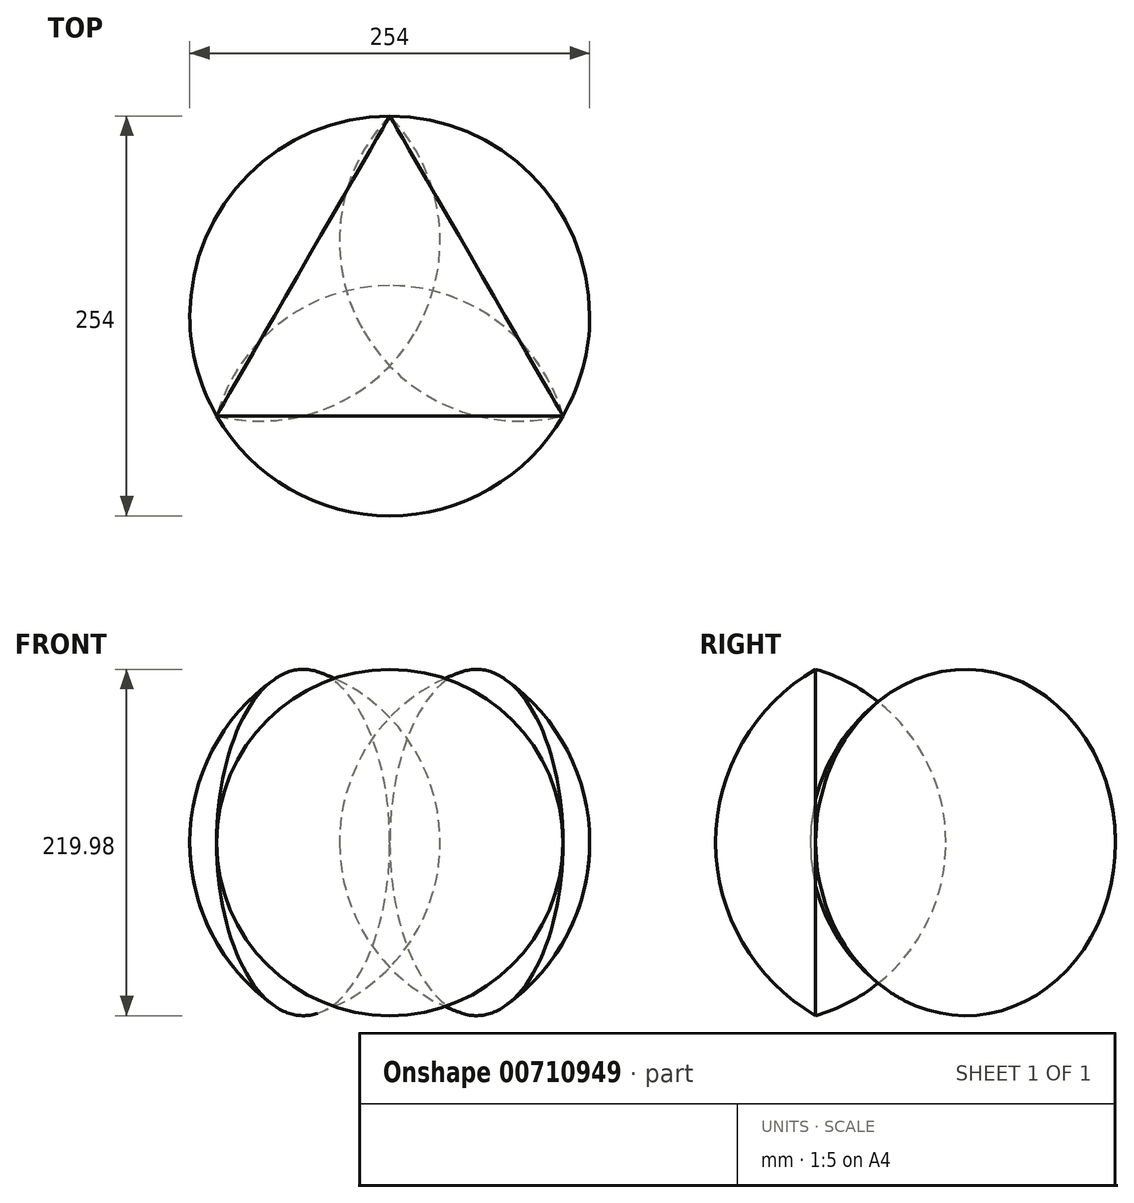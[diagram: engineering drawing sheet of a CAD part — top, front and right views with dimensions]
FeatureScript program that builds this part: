
annotation { "Feature Type Name" : "Feature", "Feature Type Description" : "" }
export const myFeature = defineFeature(function(context is Context, id is Id, definition is map)
    precondition{}
    {
        {
            var Q0;
            Q0=qCreatedBy(makeId("Front.planeOp"),FACE);
            var sketch = newSketch(context, id + "F0", { "sketchPlane" : qUnion([Q0])});
            skArc(sketch, "E0", {"start": v(95.25, 0) * mm, "mid": v(0, 95.25) * mm, "end": v(-95.25, 0) * mm});
            skLineSegment(sketch, "E1", {"start": v(-95.25, 0) * mm, "end": v(95.25, 0) * mm});
            skSolve(sketch);
        }
        {
            var Q0;
            Q0=qCreatedBy(makeId("Top.planeOp"),FACE);
            var sketch = newSketch(context, id + "F1", { "sketchPlane" : qUnion([Q0])});
            skLineSegment(sketch, "E2", {"start": v(0, 0) * mm, "end": v(74.22, 42.85) * mm});
            skSolve(sketch);
        }
        {
            var Q0;
            Q0=qCreatedBy(makeId("Front.planeOp"),FACE);
            var sketch = newSketch(context, id + "F2", { "sketchPlane" : qUnion([Q0])});
            skLineSegment(sketch, "E3", {"start": v(0, 0) * mm, "end": v(0, 72.31) * mm});
            skSolve(sketch);
        }
        {
            var Q0;
            Q0=sQuery(id+"F1.wireOp",VERTEX,"E2.end");
            var Q1;
            Q1=sQuery(id+"F2.wireOp",VERTEX,"E3.start");
            var Q2;
            Q2=sQuery(id+"F2.wireOp",VERTEX,"E3.end");
            cPlane(context, id + "F3", {"entities" : qUnion([Q0, Q1, Q2]), "cplaneType" : CPlaneType.THREE_POINT, "offset" : 25.4 * mm, "width" : 152.4 * mm, "height" : 152.4 * mm});
        }
        {
            var Q0;
            Q0=qCreatedBy(makeId("Top.planeOp"),FACE);
            var sketch = newSketch(context, id + "F4", { "sketchPlane" : qUnion([Q0])});
            skArc(sketch, "E4", {"start": v(181.63, 104.86) * mm, "mid": v(25.25, 146.76) * mm, "end": v(-16.65, -9.61) * mm});
            skLineSegment(sketch, "E5", {"start": v(0, 0) * mm, "end": v(82.49, 47.62) * mm, "construction": true});
            skCircle(sketch, "E6", {"center": v(0, 0) * mm, "radius": 127 * mm, "construction": true});
            skLineSegment(sketch, "E7", {"start": v(0, 0) * mm, "end": v(0, 127) * mm, "construction": true});
            skLineSegment(sketch, "E8", {"start": v(-16.65, -9.61) * mm, "end": v(181.63, 104.86) * mm});
            skSolve(sketch);
        }
        {
            var Q0;
            Q0 = qSketchRegion(id + "F4", true);
            var Q1;
            Q1=sQuery(id+"F4.wireOp",EDGE,"E8");
            revolve(context, id + "F5", {"surfaceOperationType" : NewSurfaceOperationType.NEW, "entities" : qUnion([Q0]), "axis" : qUnion([Q1]), "revolveType" : RevolveType.FULL});
        }
        {
            var Q0;
            Q0=makeQuery(id+"F5.opRevolve","SWEPT_BODY",BODY,{"disambiguationData":[OSD([sQuery(id+"F4.wireOp",EDGE,"E4"),sQuery(id+"F4.wireOp",EDGE,"E8")])]});
            var Q1;
            Q1=sQuery(id+"F2.wireOp",EDGE,"E3");
            circularPattern(context, id + "F6", {"entities" : qUnion([Q0]), "axis" : qUnion([Q1]), "angle" : 360 * degree, "instanceCount" : 3, "equalSpace" : true});
        }
        {
            var Q0;
            Q0=qCreatedBy(makeId("Top.planeOp"),FACE);
            var sketch = newSketch(context, id + "F7", { "sketchPlane" : qUnion([Q0])});
            skCircle(sketch, "E9", {"center": v(0, 0) * mm, "radius": 127 * mm});
            skCircle(sketch, "E10", {"center": v(0, 0) * mm, "radius": 254 * mm});
            skSolve(sketch);
        }
        {
            var Q0;
            Q0 = qSketchRegion(id + "F7", true);
            extrude(context, id + "F8", {"entities" : qUnion([Q0]), "operationType" : NewBodyOperationType.REMOVE, "endBound" : BoundingType.SYMMETRIC, "depth" : 508 * mm, "offsetDistance" : 25.4 * mm});
        }
        {
            var Q0;
            Q0=qCreatedBy(makeId("Front.planeOp"),FACE);
            var sketch = newSketch(context, id + "F9", { "sketchPlane" : qUnion([Q0])});
            skArc(sketch, "E11", {"start": v(127, 0) * mm, "mid": v(0, 127) * mm, "end": v(-127, 0) * mm});
            skLineSegment(sketch, "E12", {"start": v(-127, 0) * mm, "end": v(127, 0) * mm});
            skSolve(sketch);
        }
        {
            var Q0;
            Q0 = qSketchRegion(id + "F9", true);
            var Q1;
            Q1=sQuery(id+"F0.wireOp",EDGE,"E1");
            revolve(context, id + "F10", {"operationType" : NewBodyOperationType.INTERSECT, "surfaceOperationType" : NewSurfaceOperationType.NEW, "entities" : qUnion([Q0]), "axis" : qUnion([Q1]), "revolveType" : RevolveType.FULL});
        }
    });
